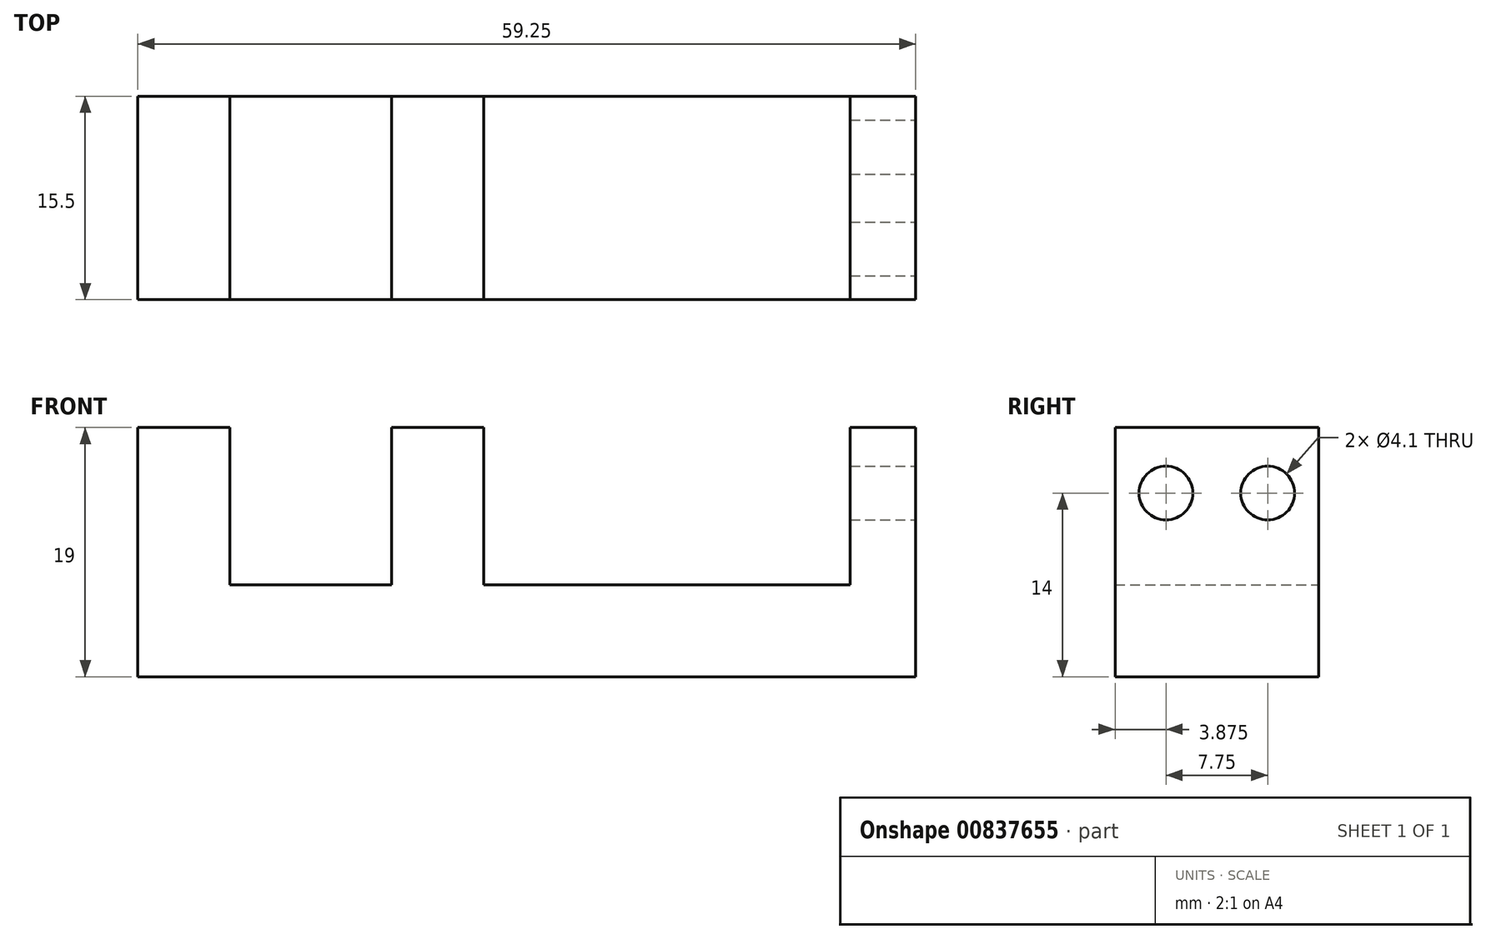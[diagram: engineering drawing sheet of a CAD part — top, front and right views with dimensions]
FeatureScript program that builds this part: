
annotation { "Feature Type Name" : "Feature", "Feature Type Description" : "" }
export const myFeature = defineFeature(function(context is Context, id is Id, definition is map)
    precondition{}
    {
        {
            var Q0;
            Q0=qCreatedBy(makeId("Top.planeOp"),FACE);
            var sketch = newSketch(context, id + "F0", { "sketchPlane" : qUnion([Q0])});
            skLineSegment(sketch, "E0.bottom", {"start": v(-31.2, -7.75) * mm, "end": v(-83.45, -7.75) * mm});
            skLineSegment(sketch, "E0.top", {"start": v(-31.2, 7.75) * mm, "end": v(-83.45, 7.75) * mm});
            skLineSegment(sketch, "E0.left", {"start": v(-31.2, -7.75) * mm, "end": v(-31.2, 7.75) * mm});
            skLineSegment(sketch, "E0.right", {"start": v(-83.45, -7.75) * mm, "end": v(-83.45, 7.75) * mm});
            skPoint(sketch, "E0.middle", {"position": v(-57.33, 0) * mm});
            skLineSegment(sketch, "E1.bottom", {"start": v(-90.45, 7.75) * mm, "end": v(-83.45, 7.75) * mm});
            skLineSegment(sketch, "E1.top", {"start": v(-90.45, -7.75) * mm, "end": v(-83.45, -7.75) * mm});
            skLineSegment(sketch, "E1.left", {"start": v(-83.45, 7.75) * mm, "end": v(-83.45, -7.75) * mm});
            skLineSegment(sketch, "E1.right", {"start": v(-90.45, 7.75) * mm, "end": v(-90.45, -7.75) * mm});
            skLineSegment(sketch, "E2.bottom", {"start": v(-71.11, 7.75) * mm, "end": v(-64.11, 7.75) * mm});
            skLineSegment(sketch, "E2.top", {"start": v(-71.11, -7.75) * mm, "end": v(-64.11, -7.75) * mm});
            skLineSegment(sketch, "E2.left", {"start": v(-71.11, 7.75) * mm, "end": v(-71.11, -7.75) * mm});
            skLineSegment(sketch, "E2.right", {"start": v(-64.11, 7.75) * mm, "end": v(-64.11, -7.75) * mm});
            skLineSegment(sketch, "E3", {"start": v(-36.2, 7.75) * mm, "end": v(-36.2, -7.75) * mm});
            skSolve(sketch);
        }
        {
            var Q0;
            Q0=makeQuery(id+"F0.imprint","IMPRINT",FACE,{"disambiguationData":[TD([[makeQuery(id+"F0.imprint","IMPRINT",EDGE,{"derivedFrom":sQuery(id+"F0.wireOp",EDGE,"E0.right")}),1.0]])]});
            var Q1;
            {var subQ0=sQuery(id+"F0.wireOp",EDGE,"E0.right");Q1=makeQuery(id+"F0.imprint","IMPRINT",FACE,{"disambiguationData":[TD([[makeQuery(id+"F0.imprint","IMPRINT",EDGE,{"derivedFrom":subQ0}),-1.0]])]});}
            var Q2;
            {var subQ0=sQuery(id+"F0.wireOp",EDGE,"E2.left");Q2=makeQuery(id+"F0.imprint","IMPRINT",FACE,{"disambiguationData":[TD([[makeQuery(id+"F0.imprint","IMPRINT",EDGE,{"derivedFrom":subQ0}),1.0]])]});}
            var Q3;
            {var subQ2=sQuery(id+"F0.wireOp",EDGE,"E2.right");Q3=makeQuery(id+"F0.imprint","IMPRINT",FACE,{"disambiguationData":[TD([[makeQuery(id+"F0.imprint","IMPRINT",EDGE,{"derivedFrom":subQ2}),1.0]])]});}
            var Q4;
            {var subQ2=sQuery(id+"F0.wireOp",EDGE,"E0.left");Q4=makeQuery(id+"F0.imprint","IMPRINT",FACE,{"disambiguationData":[TD([[makeQuery(id+"F0.imprint","IMPRINT",EDGE,{"derivedFrom":subQ2}),1.0]])]});}
            extrude(context, id + "F1", {"entities" : qUnion([Q0, Q1, Q2, Q3, Q4]), "depth" : 7 * mm, "offsetDistance" : 25 * mm});
        }
        {
            var Q0;
            Q0=makeQuery(id+"F0.imprint","IMPRINT",FACE,{"disambiguationData":[TD([[makeQuery(id+"F0.imprint","IMPRINT",EDGE,{"derivedFrom":sQuery(id+"F0.wireOp",EDGE,"E0.right")}),1.0]])]});
            var Q1;
            {var subQ0=sQuery(id+"F0.wireOp",EDGE,"E2.left");Q1=makeQuery(id+"F0.imprint","IMPRINT",FACE,{"disambiguationData":[TD([[makeQuery(id+"F0.imprint","IMPRINT",EDGE,{"derivedFrom":subQ0}),1.0]])]});}
            var Q2;
            {var subQ2=sQuery(id+"F0.wireOp",EDGE,"E0.left");Q2=makeQuery(id+"F0.imprint","IMPRINT",FACE,{"disambiguationData":[TD([[makeQuery(id+"F0.imprint","IMPRINT",EDGE,{"derivedFrom":subQ2}),1.0]])]});}
            extrude(context, id + "F2", {"entities" : qUnion([Q0, Q1, Q2]), "operationType" : NewBodyOperationType.ADD, "depth" : 19 * mm, "offsetDistance" : 25 * mm});
        }
        {
            var Q0;
            {var subQ0=sQuery(id+"F0.wireOp",EDGE,"E0.left");Q0=makeQuery(id+"F2.boolean.opBoolean","MERGE",FACE,{"derivedFrom":[makeQuery(id+"F1.opExtrude","SWEPT_FACE",FACE,{"disambiguationData":[OSD([subQ0])]}),makeQuery(id+"F2.opExtrude","SWEPT_FACE",FACE,{"disambiguationData":[OSD([subQ0])]})]});}
            var sketch = newSketch(context, id + "F3", { "sketchPlane" : qUnion([Q0])});
            skLineSegment(sketch, "E4", {"start": v(0, 19) * mm, "end": v(0, 0) * mm});
            skLineSegment(sketch, "E5", {"start": v(-7.75, 14) * mm, "end": v(7.75, 14) * mm});
            skPoint(sketch, "E6", {"position": v(0, 14) * mm});
            skPoint(sketch, "E7", {"position": v(-7.75, 14) * mm});
            skPoint(sketch, "E8", {"position": v(0, 19) * mm});
            skPoint(sketch, "E9", {"position": v(7.75, 14) * mm});
            skPoint(sketch, "E10", {"position": v(-3.88, 14) * mm});
            skPoint(sketch, "E11", {"position": v(3.87, 14) * mm});
            skCircle(sketch, "E12", {"center": v(-3.88, 14) * mm, "radius": 2.05 * mm});
            skCircle(sketch, "E13", {"center": v(3.87, 14) * mm, "radius": 2.05 * mm});
            skSolve(sketch);
        }
        {
            var Q0;
            {var subQ0=sQuery(id+"F3.wireOp",EDGE,"E12");var subQ1=sQuery(id+"F3.wireOp",EDGE,"E5");var subQ2=makeQuery(id+"F3.imprint","INTERSECT",VERTEX,{"disambiguationData":[OD(0.0)],"derivedFrom":[subQ1,subQ0]});Q0=makeQuery(id+"F3.imprint","IMPRINT",FACE,{"disambiguationData":[TD([[makeQuery(id+"F3.imprint","IMPRINT",EDGE,{"disambiguationData":[TD([[subQ2,-1.0]])],"derivedFrom":subQ1}),1.0]])]});}
            var Q1;
            {var subQ0=sQuery(id+"F3.wireOp",EDGE,"E13");var subQ1=sQuery(id+"F3.wireOp",EDGE,"E5");var subQ2=makeQuery(id+"F3.imprint","INTERSECT",VERTEX,{"disambiguationData":[OD(0.0)],"derivedFrom":[subQ1,subQ0]});Q1=makeQuery(id+"F3.imprint","IMPRINT",FACE,{"disambiguationData":[TD([[makeQuery(id+"F3.imprint","IMPRINT",EDGE,{"disambiguationData":[TD([[subQ2,-1.0]])],"derivedFrom":subQ1}),1.0]])]});}
            var Q2;
            {var subQ0=sQuery(id+"F3.wireOp",EDGE,"E13");var subQ1=sQuery(id+"F3.wireOp",EDGE,"E5");var subQ2=makeQuery(id+"F3.imprint","INTERSECT",VERTEX,{"disambiguationData":[OD(0.0)],"derivedFrom":[subQ1,subQ0]});Q2=makeQuery(id+"F3.imprint","IMPRINT",FACE,{"disambiguationData":[TD([[makeQuery(id+"F3.imprint","IMPRINT",EDGE,{"disambiguationData":[TD([[subQ2,-1.0]])],"derivedFrom":subQ1}),-1.0]])]});}
            var Q3;
            {var subQ0=sQuery(id+"F3.wireOp",EDGE,"E12");var subQ1=sQuery(id+"F3.wireOp",EDGE,"E5");var subQ2=makeQuery(id+"F3.imprint","INTERSECT",VERTEX,{"disambiguationData":[OD(0.0)],"derivedFrom":[subQ1,subQ0]});Q3=makeQuery(id+"F3.imprint","IMPRINT",FACE,{"disambiguationData":[TD([[makeQuery(id+"F3.imprint","IMPRINT",EDGE,{"disambiguationData":[TD([[subQ2,-1.0]])],"derivedFrom":subQ1}),-1.0]])]});}
            extrude(context, id + "F4", {"entities" : qUnion([Q0, Q1, Q2, Q3]), "operationType" : NewBodyOperationType.REMOVE, "oppositeDirection" : true, "depth" : 25 * mm, "offsetDistance" : 25 * mm});
        }
    });
